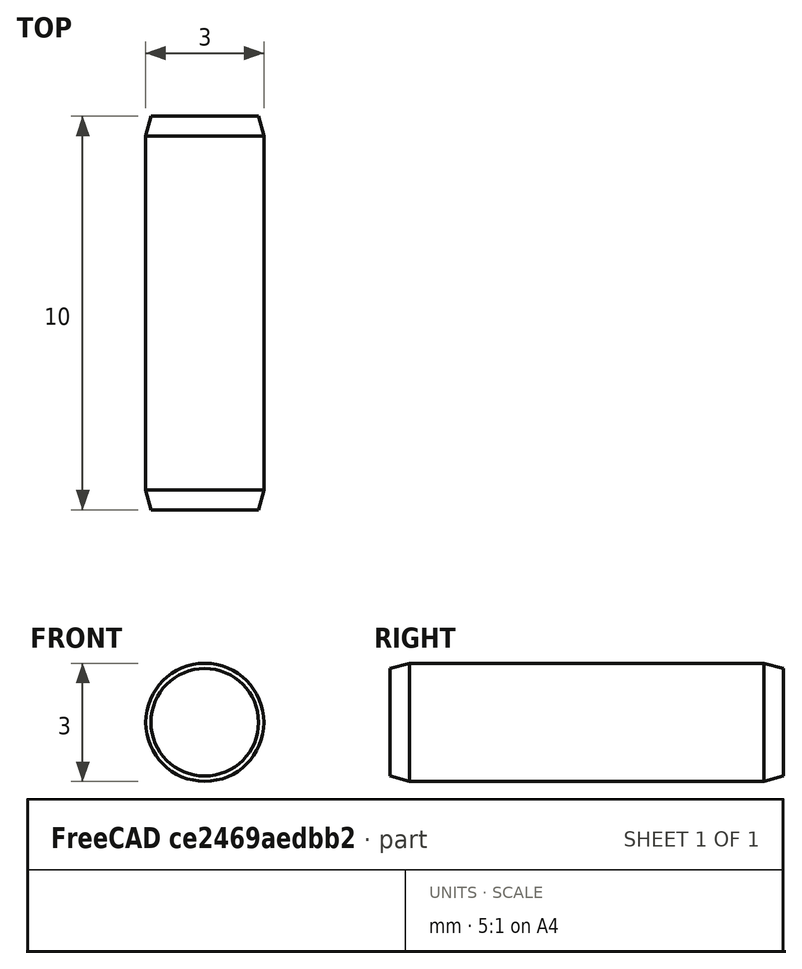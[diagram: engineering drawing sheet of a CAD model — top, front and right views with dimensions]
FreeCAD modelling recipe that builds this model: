
FCSTD DOCUMENT  (FreeCAD 0.15R4470 (Git))
Label: Zyl-Stift_ISO_2338-3x10
License: CC-BY 3.0
LicenseURL: http://creativecommons.org/licenses/by/3.0/
objects: Sketcher::SketchObject×1, PartDesign::Revolution×1
note: 3 computed .brp shape members not serialized (recipe doc carries the construction recipe); baked Part::Feature solids carry a one-line shape summary decoded from their .brp

FEATURE [Sketcher::SketchObject] Sketch
  Placement = pos=(0,0,0) rot=(0.57735,0.57735,0.57735;2.0944rad)
  sketch-geometry (7):
    g0: LineSegment StartX=0 StartY=0 StartZ=0 EndX=0 EndY=1.36603 EndZ=0
    g1: LineSegment StartX=0 StartY=1.36603 StartZ=0 EndX=0.5 EndY=1.5 EndZ=0
    g2: LineSegment StartX=0.5 StartY=1.5 StartZ=0 EndX=9.5 EndY=1.5 EndZ=0
    g3: LineSegment StartX=9.5 StartY=1.5 StartZ=0 EndX=10 EndY=1.36603 EndZ=0
    g4: LineSegment StartX=10 StartY=1.36603 StartZ=0 EndX=10 EndY=0 EndZ=0
    g5: LineSegment StartX=10 StartY=0 StartZ=0 EndX=0 EndY=0 EndZ=0
    g6: LineSegment [constr] StartX=0 StartY=1.36603 StartZ=0 EndX=10 EndY=1.36603 EndZ=0
  constraints (19):
    c: Coincident(g0,g-1)
    c: PointOnObject(g0,g-2)
    c: Coincident(g0,g1)
    c: Coincident(g1,g2)
    c: Horizontal(g2)
    c: Coincident(g2,g3)
    c: Coincident(g3,g4)
    c: Vertical(g4)
    c: Coincident(g4,g5)
    c: Coincident(g5,g-1)
    c: Horizontal(g5)
    c: Equal(g3,g1)
    c: Coincident(g6,g0)
    c: Coincident(g6,g3)
    c: Horizontal(g6)
    c: Angle(g6,g1) = 0.261799
    c: DistanceY(g-1,g1) = 1.5
    c: DistanceX(g5) = -10
    c: DistanceX(g1) = 0.5
FEATURE [PartDesign::Revolution] Revolution  label="Zyl-Stift ISO 2338-3x10 #"
  Angle = 360
  Axis = (0,1,0)
  Base = (0,0,0)
  Placement = pos=(0,0,0) rot=(0.57735,0.57735,0.57735;2.0944rad)
  ReferenceAxis = -> Sketch [H_Axis]
  Sketch = -> Sketch
